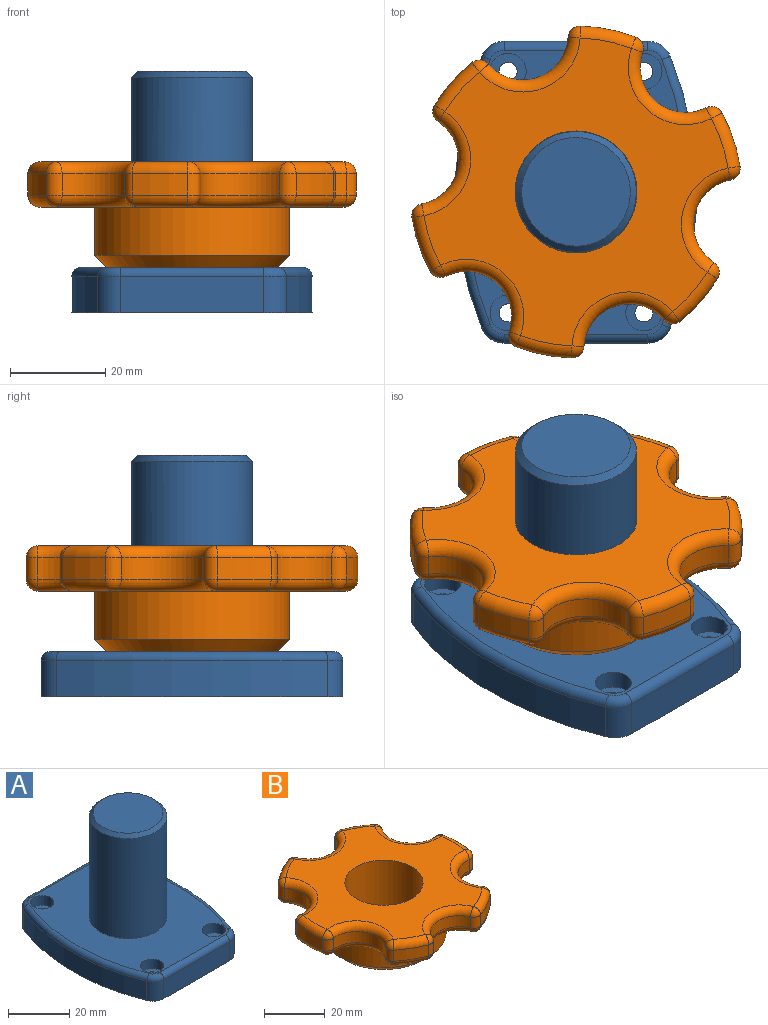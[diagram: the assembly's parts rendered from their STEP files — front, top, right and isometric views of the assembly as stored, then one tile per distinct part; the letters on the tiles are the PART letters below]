
ASSEMBLY  parts=2 mates=1
PART A: 33 faces, bbox 63.4x64.3x50.8 mm
  f0: cylinder r=12.7mm len=40.01mm, axis (0,0,-1), area 3192.3mm2, adj f2,f6
  f1: plane 22.86x22.86mm, normal (0,0,1), area 410.4mm2, adj f2
  f2: cone r=12.7mm half-angle=45deg, axis (0,0,-1), area 136.2mm2, adj f0,f1
  f3: plane 30.26x7.62mm, normal (0,-1,0), area 230.6mm2, adj f8,f22,f24,f32
  f4: plane 30.26x7.62mm, normal (0,1,0), area 230.6mm2, adj f8,f21,f23,f25
  f5: cylinder r=76.2mm len=57.15mm, axis (0,0,-1), area 446.4mm2, adj f8,f23,f24,f29
  f6: plane 59.69x46.99mm, normal (0,0,1), area 1867.9mm2, adj f0,f11,f14,f17,f20,f25,f26,f27
  f7: cylinder r=76.2mm len=57.15mm, axis (0,0,-1), area 446.4mm2, adj f8,f21,f22,f28
  f8: plane 63.5x50.8mm, normal (0,0,-1), area 2884.4mm2, adj f3,f4,f5,f7,f9,f12,f15,f18
  f9: cylinder r=1.91mm len=5.72mm, axis (0,0,1), area 68.4mm2, adj f8,f10
  f10: plane 7.62x7.62mm, normal (0,0,1), area 34.2mm2, adj f9,f11
  f11: cylinder r=3.81mm len=7.62mm, axis (0,0,1), area 91.2mm2, adj f6,f10
  f12: cylinder r=1.91mm len=5.72mm, axis (0,0,1), area 68.4mm2, adj f8,f13
  f13: plane 7.62x7.62mm, normal (0,0,1), area 34.2mm2, adj f12,f14
  f14: cylinder r=3.81mm len=7.62mm, axis (0,0,1), area 91.2mm2, adj f6,f13
  f15: cylinder r=1.91mm len=5.72mm, axis (0,0,1), area 68.4mm2, adj f8,f16
  f16: plane 7.62x7.62mm, normal (0,0,1), area 34.2mm2, adj f15,f17
  f17: cylinder r=3.81mm len=7.62mm, axis (0,0,1), area 91.2mm2, adj f6,f16
  f18: cylinder r=1.91mm len=5.72mm, axis (0,0,1), area 68.4mm2, adj f8,f19
  f19: plane 7.62x7.62mm, normal (0,0,1), area 34.2mm2, adj f18,f20
  f20: cylinder r=3.81mm len=7.62mm, axis (0,0,1), area 91.2mm2, adj f6,f19
  f21: cylinder r=5.08mm len=7.62mm, axis (0,0,-1), area 45.9mm2, adj f4,f7,f8,f26
  f22: cylinder r=5.08mm len=7.62mm, axis (0,0,-1), area 45.9mm2, adj f3,f7,f8,f30
  f23: cylinder r=5.08mm len=7.62mm, axis (0,0,-1), area 45.9mm2, adj f4,f5,f8,f27
  f24: cylinder r=5.08mm len=7.62mm, axis (0,0,-1), area 45.9mm2, adj f3,f5,f8,f31
  f25: cylinder r=1.91mm len=30.26mm, axis (1,0,0), area 90.5mm2, adj f4,f6,f26,f27
  f26: torus R=3.17mm, axis (0,0,1), area 15.6mm2, adj f6,f21,f25,f28
  f27: torus R=3.17mm, axis (0,0,1), area 15.6mm2, adj f6,f23,f25,f29
  f28: torus R=74.3mm, axis (0,0,1), area 173.7mm2, adj f6,f7,f26,f30
  f29: torus R=74.3mm, axis (0,0,1), area 173.7mm2, adj f5,f6,f27,f31
  f30: torus R=3.17mm, axis (0,0,1), area 15.6mm2, adj f6,f22,f28,f32
  f31: torus R=3.17mm, axis (0,0,1), area 15.6mm2, adj f6,f24,f29,f32
  f32: cylinder r=1.91mm len=30.26mm, axis (-1,0,0), area 90.5mm2, adj f3,f6,f30,f31
PART B: 78 faces, bbox 70.9x66.5x22.2 mm
  f0: plane 64.77x60.79mm, normal (0,0,1), area 1867.1mm2, adj f8,f30,f33,f34,f37,f38,f41,f42
  f1: cylinder r=34.92mm len=11.89mm, axis (0,0,-1), area 53.1mm2, adj f26,f28,f37,f61
  f2: cylinder r=34.92mm len=10.3mm, axis (0,0,-1), area 53.1mm2, adj f23,f25,f45,f69
  f3: cylinder r=34.92mm len=10.3mm, axis (0,0,-1), area 53.1mm2, adj f20,f22,f53,f77
  f4: cylinder r=34.92mm len=11.89mm, axis (0,0,-1), area 53.1mm2, adj f17,f19,f46,f70
  f5: cylinder r=34.92mm len=10.3mm, axis (0,0,-1), area 53.1mm2, adj f14,f16,f38,f62
  f6: plane 64.77x60.79mm, normal (0,0,-1), area 1070.6mm2, adj f10,f54,f57,f58,f61,f62,f65,f66
  f7: cylinder r=34.92mm len=10.3mm, axis (0,0,-1), area 53.1mm2, adj f13,f29,f30,f54
  f8: cylinder r=12.83mm len=25.65mm, axis (0,0,-1), area 1791.2mm2, adj f0,f9
  f9: plane 35.81x35.81mm, normal (0,0,-1), area 490.5mm2, adj f8,f11
  f10: cylinder r=20.45mm len=40.89mm, axis (0,0,-1), area 1305.3mm2, adj f6,f11
  f11: cone r=17.91mm half-angle=45deg, axis (0,0,1), area 432.8mm2, adj f9,f10
  f12: cylinder r=9.53mm len=17.66mm, axis (0,0,1), area 100.4mm2, adj f13,f14,f34,f58
  f13: cylinder r=2.54mm len=4.45mm, axis (0,0,1), area 17.4mm2, adj f7,f12,f32,f56
  f14: cylinder r=2.54mm len=4.45mm, axis (0,0,-1), area 17.4mm2, adj f5,f12,f36,f60
  f15: cylinder r=9.53mm len=15.38mm, axis (0,0,1), area 100.4mm2, adj f16,f17,f42,f66
  f16: cylinder r=2.54mm len=4.45mm, axis (0,0,1), area 17.4mm2, adj f5,f15,f40,f64
  f17: cylinder r=2.54mm len=4.45mm, axis (0,0,-1), area 17.4mm2, adj f4,f15,f44,f68
  f18: cylinder r=9.53mm len=15.38mm, axis (0,0,1), area 100.4mm2, adj f19,f20,f50,f74
  f19: cylinder r=2.54mm len=4.45mm, axis (0,0,1), area 17.4mm2, adj f4,f18,f48,f72
  f20: cylinder r=2.54mm len=4.45mm, axis (0,0,-1), area 17.4mm2, adj f3,f18,f52,f76
  f21: cylinder r=9.53mm len=17.66mm, axis (0,0,1), area 100.4mm2, adj f22,f23,f49,f73
  f22: cylinder r=2.54mm len=4.45mm, axis (0,0,1), area 17.4mm2, adj f3,f21,f51,f75
  f23: cylinder r=2.54mm len=4.45mm, axis (0,0,-1), area 17.4mm2, adj f2,f21,f47,f71
  f24: cylinder r=9.53mm len=15.38mm, axis (0,0,1), area 100.4mm2, adj f25,f26,f41,f65
  f25: cylinder r=2.54mm len=4.45mm, axis (0,0,1), area 17.4mm2, adj f2,f24,f43,f67
  f26: cylinder r=2.54mm len=4.45mm, axis (0,0,-1), area 17.4mm2, adj f1,f24,f39,f63
  f27: cylinder r=9.53mm len=15.38mm, axis (0,0,1), area 100.4mm2, adj f28,f29,f33,f57
  f28: cylinder r=2.54mm len=4.45mm, axis (0,0,1), area 17.4mm2, adj f1,f27,f35,f59
  f29: cylinder r=2.54mm len=4.45mm, axis (0,0,-1), area 17.4mm2, adj f7,f27,f31,f55
  f30: torus R=32.38mm, axis (0,0,-1), area 46.4mm2, adj f0,f7,f31,f32
  f31: sphere r=2.54mm, area 9.9mm2, adj f29,f30,f33
  f32: sphere r=2.54mm, area 9.9mm2, adj f13,f30,f34
  f33: torus R=12.06mm, axis (0,0,-1), area 98.9mm2, adj f0,f27,f31,f35
  f34: torus R=12.06mm, axis (0,0,-1), area 98.9mm2, adj f0,f12,f32,f36
  f35: sphere r=2.54mm, area 9.9mm2, adj f28,f33,f37
  f36: sphere r=2.54mm, area 9.9mm2, adj f14,f34,f38
  f37: torus R=32.38mm, axis (0,0,-1), area 46.4mm2, adj f0,f1,f35,f39
  f38: torus R=32.38mm, axis (0,0,-1), area 46.4mm2, adj f0,f5,f36,f40
  f39: sphere r=2.54mm, area 9.9mm2, adj f26,f37,f41
  f40: sphere r=2.54mm, area 9.9mm2, adj f16,f38,f42
  f41: torus R=12.06mm, axis (0,0,-1), area 98.9mm2, adj f0,f24,f39,f43
  f42: torus R=12.06mm, axis (0,0,-1), area 98.9mm2, adj f0,f15,f40,f44
  f43: sphere r=2.54mm, area 9.9mm2, adj f25,f41,f45
  f44: sphere r=2.54mm, area 9.9mm2, adj f17,f42,f46
  f45: torus R=32.38mm, axis (0,0,-1), area 46.4mm2, adj f0,f2,f43,f47
  f46: torus R=32.38mm, axis (0,0,-1), area 46.4mm2, adj f0,f4,f44,f48
  f47: sphere r=2.54mm, area 9.9mm2, adj f23,f45,f49
  f48: sphere r=2.54mm, area 9.9mm2, adj f19,f46,f50
  f49: torus R=12.06mm, axis (0,0,-1), area 98.9mm2, adj f0,f21,f47,f51
  f50: torus R=12.06mm, axis (0,0,-1), area 98.9mm2, adj f0,f18,f48,f52
  f51: sphere r=2.54mm, area 9.9mm2, adj f22,f49,f53
  f52: sphere r=2.54mm, area 9.9mm2, adj f20,f50,f53
  f53: torus R=32.38mm, axis (0,0,-1), area 46.4mm2, adj f0,f3,f51,f52
  f54: torus R=32.38mm, axis (0,0,-1), area 46.4mm2, adj f6,f7,f55,f56
  f55: sphere r=2.54mm, area 9.9mm2, adj f29,f54,f57
  f56: sphere r=2.54mm, area 9.9mm2, adj f13,f54,f58
  f57: torus R=12.06mm, axis (0,0,-1), area 98.9mm2, adj f6,f27,f55,f59
  f58: torus R=12.06mm, axis (0,0,-1), area 98.9mm2, adj f6,f12,f56,f60
  f59: sphere r=2.54mm, area 9.9mm2, adj f28,f57,f61
  f60: sphere r=2.54mm, area 9.9mm2, adj f14,f58,f62
  f61: torus R=32.38mm, axis (0,0,-1), area 46.4mm2, adj f1,f6,f59,f63
  f62: torus R=32.38mm, axis (0,0,-1), area 46.4mm2, adj f5,f6,f60,f64
  f63: sphere r=2.54mm, area 9.9mm2, adj f26,f61,f65
  f64: sphere r=2.54mm, area 9.9mm2, adj f16,f62,f66
  f65: torus R=12.06mm, axis (0,0,-1), area 98.9mm2, adj f6,f24,f63,f67
  f66: torus R=12.06mm, axis (0,0,-1), area 98.9mm2, adj f6,f15,f64,f68
  f67: sphere r=2.54mm, area 9.9mm2, adj f25,f65,f69
  f68: sphere r=2.54mm, area 9.9mm2, adj f17,f66,f70
  f69: torus R=32.38mm, axis (0,0,-1), area 46.4mm2, adj f2,f6,f67,f71
  f70: torus R=32.38mm, axis (0,0,-1), area 46.4mm2, adj f4,f6,f68,f72
  f71: sphere r=2.54mm, area 9.9mm2, adj f23,f69,f73
  f72: sphere r=2.54mm, area 9.9mm2, adj f19,f70,f74
  f73: torus R=12.06mm, axis (0,0,-1), area 98.9mm2, adj f6,f21,f71,f75
  f74: torus R=12.06mm, axis (0,0,-1), area 98.9mm2, adj f6,f18,f72,f76
  f75: sphere r=2.54mm, area 9.9mm2, adj f22,f73,f77
  f76: sphere r=2.54mm, area 9.9mm2, adj f20,f74,f77
  f77: torus R=32.38mm, axis (0,0,-1), area 46.4mm2, adj f3,f6,f75,f76
PLACE A t=(-2.37,12.78,-4.17)mm fixed
PLACE B rot(axis=(0,0,-1),161.3deg) t=(-2.37,12.78,5.35)mm
MATE cylindrical A.f0 <-> B.f1  axis (0,0,1) through (-2.37,12.78,46.63)mm
